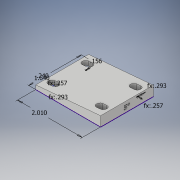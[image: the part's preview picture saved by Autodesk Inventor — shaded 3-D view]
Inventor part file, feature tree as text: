
AUTODESK INVENTOR PART (.ipt)
format: ipt  version: 2018 (Build 220112000, 112)  size: 201,728 bytes
history: native  units: in
note: dims shown in document units (in); Inventor stores cm internally (conversion verified against a paired STEP export)
features: sketch x4, extrude x3, projected_geometry x1
ambient origin geometry x8: Origin, YZ Plane, XZ Plane, XY Plane, X Axis, Y Axis, Z Axis, Center Point
bodies: Body1 (feature_tree)
feature tree (8):
  sketch  "Sketch1"  dims[d0=0.1562in d1=1.64in]
  extrude  "Extrusion8"  Depth=1.64in
  extrude  "Extrusion9"  Depth=0.24in
  extrude  "Extrusion10"  Depth=0.257in
  sketch  "Sketch10"  dims[d2=2.01in d3=0.24in]
  sketch  "Sketch11"  dims[d4=0.293in d5=0.257in]
  sketch  "Sketch13"  dims[d6=0.293in d7=0.257in d20=0.125in d21=1.25in d22=0.125in d23=0.125in d24=0.1875in d25=0.0938in d61=0.0344in d62=0.125in d63=1.64in d64=0.0in d65=0.125in d66=0.0995in d67=1.64in d68=0.0in d69=0.08in d70=0.015in d71=0.0in]
  projected_geometry  "Projected Loop1"
